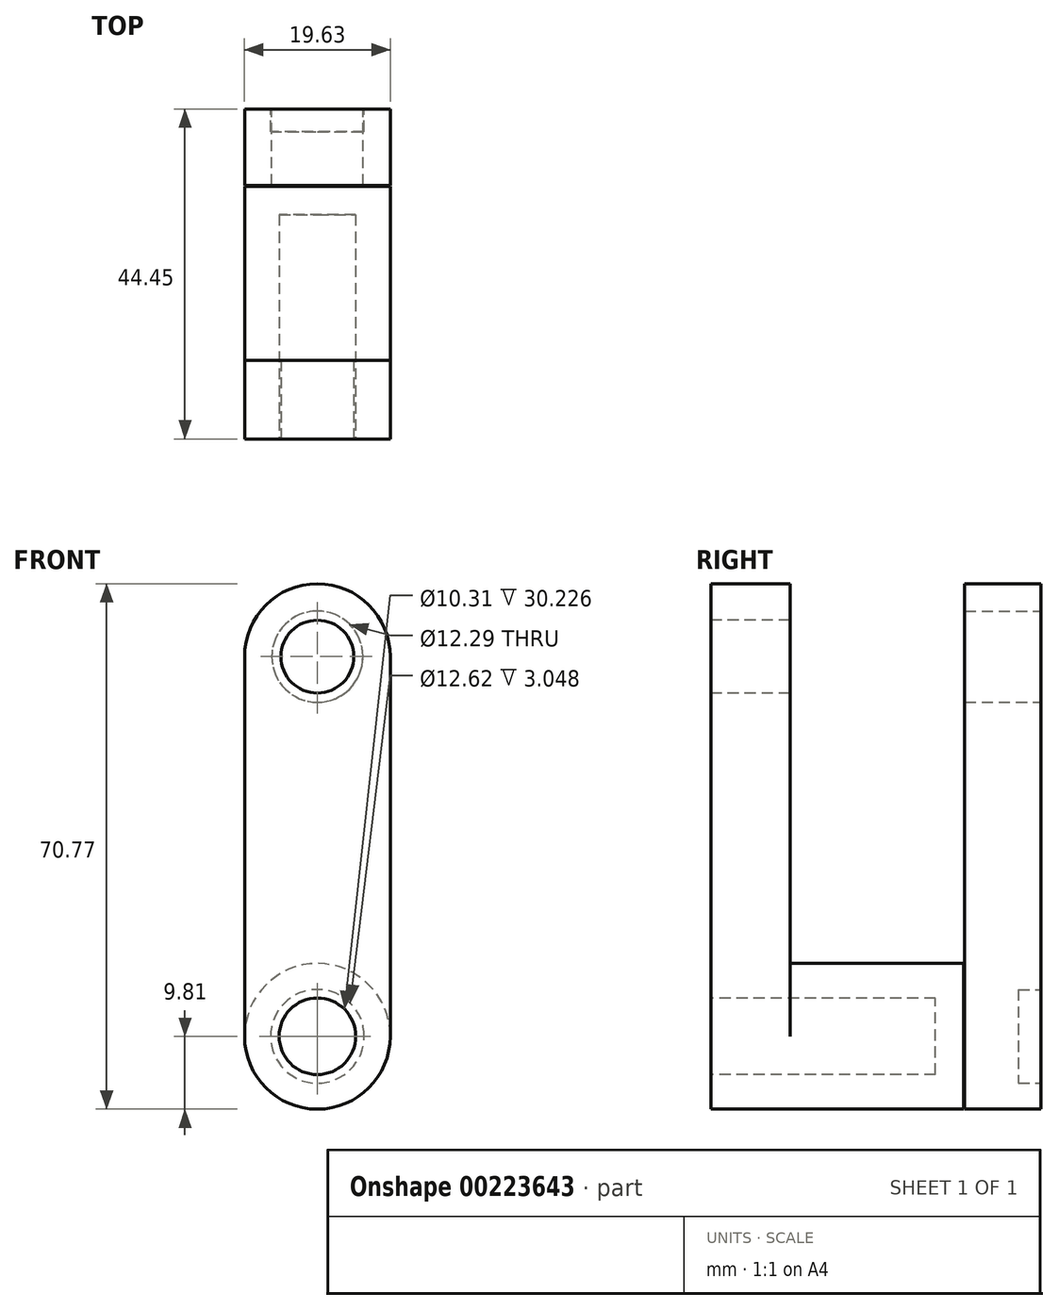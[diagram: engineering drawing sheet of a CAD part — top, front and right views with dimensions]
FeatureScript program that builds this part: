
annotation { "Feature Type Name" : "Feature", "Feature Type Description" : "" }
export const myFeature = defineFeature(function(context is Context, id is Id, definition is map)
    precondition{}
    {
        {
            var Q0;
            Q0=qCreatedBy(makeId("Front.planeOp"),FACE);
            var sketch = newSketch(context, id + "F0", { "sketchPlane" : qUnion([Q0])});
            skLineSegment(sketch, "E0", {"start": v(0, 0) * mm, "end": v(0, 51.15) * mm});
            skLineSegment(sketch, "E1", {"start": v(-19.63, 51.15) * mm, "end": v(-19.63, 0) * mm});
            skArc(sketch, "E2", {"start": v(-19.63, 51.15) * mm, "mid": v(-9.81, 60.96) * mm, "end": v(0, 51.15) * mm});
            skArc(sketch, "E3", {"start": v(-19.63, 0) * mm, "mid": v(-9.81, -9.81) * mm, "end": v(0, 0) * mm});
            skSolve(sketch);
        }
        {
            var Q0;
            Q0=makeQuery(id+"F0.imprint","IMPRINT",FACE,{"disambiguationData":[TD([[makeQuery(id+"F0.imprint","IMPRINT",EDGE,{"derivedFrom":sQuery(id+"F0.wireOp",EDGE,"E0")}),1.0]])]});
            extrude(context, id + "F1", {"entities" : qUnion([Q0]), "oppositeDirection" : true, "depth" : 44.45 * mm});
        }
        {
            var Q0;
            Q0=qCreatedBy(makeId("Right.planeOp"),FACE);
            var sketch = newSketch(context, id + "F2", { "sketchPlane" : qUnion([Q0])});
            skLineSegment(sketch, "E4.bottom", {"start": v(10.62, 64.08) * mm, "end": v(34.17, 64.08) * mm});
            skLineSegment(sketch, "E4.top", {"start": v(10.62, -13.05) * mm, "end": v(34.17, -13.05) * mm});
            skLineSegment(sketch, "E4.left", {"start": v(10.62, 64.08) * mm, "end": v(10.62, -13.05) * mm});
            skLineSegment(sketch, "E4.right", {"start": v(34.17, 64.08) * mm, "end": v(34.17, -13.05) * mm});
            skSolve(sketch);
        }
        {
            var Q0;
            Q0 = qSketchRegion(id + "F2", true);
            extrude(context, id + "F3", {"entities" : qUnion([Q0]), "operationType" : NewBodyOperationType.REMOVE, "oppositeDirection" : true, "depth" : 101.6 * mm});
        }
        {
            var Q0;
            Q0=makeQuery(id+"F1.opExtrude","CAP_FACE",FACE,{"disambiguationData":[OSD([sQuery(id+"F0.wireOp",EDGE,"E0"),sQuery(id+"F0.wireOp",EDGE,"E1"),sQuery(id+"F0.wireOp",EDGE,"E2"),sQuery(id+"F0.wireOp",EDGE,"E3")])],"isStart":true});
            var sketch = newSketch(context, id + "F4", { "sketchPlane" : qUnion([Q0])});
            skCircle(sketch, "E5", {"center": v(-9.81, 0) * mm, "radius": 4.02 * mm});
            skCircle(sketch, "E6", {"center": v(-9.81, 51.15) * mm, "radius": 4.9 * mm});
            skSolve(sketch);
        }
        {
            var Q0;
            Q0=makeQuery(id+"F4.imprint","IMPRINT",FACE,{"disambiguationData":[TD([[makeQuery(id+"F4.imprint","IMPRINT",EDGE,{"derivedFrom":sQuery(id+"F4.wireOp",EDGE,"E6")}),1.0]])]});
            extrude(context, id + "F5", {"entities" : qUnion([Q0]), "operationType" : NewBodyOperationType.REMOVE, "oppositeDirection" : true, "depth" : 74.93 * mm});
        }
        {
            var Q0;
            Q0=makeQuery(id+"F1.opExtrude","CAP_FACE",FACE,{"disambiguationData":[OSD([sQuery(id+"F0.wireOp",EDGE,"E0"),sQuery(id+"F0.wireOp",EDGE,"E1"),sQuery(id+"F0.wireOp",EDGE,"E2"),sQuery(id+"F0.wireOp",EDGE,"E3")])],"isStart":true});
            var sketch = newSketch(context, id + "F6", { "sketchPlane" : qUnion([Q0])});
            skArc(sketch, "E7", {"start": v(0, 0) * mm, "mid": v(-9.81, 9.81) * mm, "end": v(-19.63, 0) * mm});
            skSolve(sketch);
        }
        {
            var Q0;
            Q0=makeQuery(id+"F6.imprint","IMPRINT",FACE,{"disambiguationData":[TD([[makeQuery(id+"F6.imprint","IMPRINT",EDGE,{"derivedFrom":sQuery(id+"F6.wireOp",EDGE,"E7")}),1.0]])]});
            extrude(context, id + "F7", {"entities" : qUnion([Q0]), "operationType" : NewBodyOperationType.ADD, "oppositeDirection" : true, "depth" : 34.04 * mm});
        }
        {
            var Q0;
            Q0=makeQuery(id+"F1.opExtrude","CAP_FACE",FACE,{"disambiguationData":[OSD([sQuery(id+"F0.wireOp",EDGE,"E0"),sQuery(id+"F0.wireOp",EDGE,"E1"),sQuery(id+"F0.wireOp",EDGE,"E2"),sQuery(id+"F0.wireOp",EDGE,"E3")])],"isStart":true});
            var sketch = newSketch(context, id + "F8", { "sketchPlane" : qUnion([Q0])});
            skCircle(sketch, "E8", {"center": v(-9.81, 0) * mm, "radius": 5.16 * mm});
            skSolve(sketch);
        }
        {
            var Q0;
            Q0=makeQuery(id+"F8.imprint","IMPRINT",FACE,{"disambiguationData":[TD([[makeQuery(id+"F8.imprint","IMPRINT",EDGE,{"derivedFrom":sQuery(id+"F8.wireOp",EDGE,"E8")}),1.0]])]});
            extrude(context, id + "F9", {"entities" : qUnion([Q0]), "operationType" : NewBodyOperationType.REMOVE, "oppositeDirection" : true, "depth" : 30.23 * mm});
        }
        {
            var Q0;
            Q0=makeQuery(id+"F1.opExtrude","CAP_FACE",FACE,{"disambiguationData":[OSD([sQuery(id+"F0.wireOp",EDGE,"E0"),sQuery(id+"F0.wireOp",EDGE,"E1"),sQuery(id+"F0.wireOp",EDGE,"E2"),sQuery(id+"F0.wireOp",EDGE,"E3")])],"isStart":false});
            var sketch = newSketch(context, id + "F10", { "sketchPlane" : qUnion([Q0])});
            skCircle(sketch, "E9", {"center": v(9.81, 51.15) * mm, "radius": 6.15 * mm});
            skCircle(sketch, "E10", {"center": v(9.81, 0) * mm, "radius": 6.14 * mm});
            skSolve(sketch);
        }
        {
            var Q0;
            Q0=makeQuery(id+"F10.imprint","IMPRINT",FACE,{"disambiguationData":[TD([[makeQuery(id+"F10.imprint","IMPRINT",EDGE,{"derivedFrom":sQuery(id+"F10.wireOp",EDGE,"E9")}),1.0]])]});
            extrude(context, id + "F11", {"entities" : qUnion([Q0]), "operationType" : NewBodyOperationType.REMOVE, "oppositeDirection" : true, "depth" : 23.62 * mm});
        }
        {
            var Q0;
            Q0=makeQuery(id+"F1.opExtrude","CAP_FACE",FACE,{"disambiguationData":[OSD([sQuery(id+"F0.wireOp",EDGE,"E0"),sQuery(id+"F0.wireOp",EDGE,"E1"),sQuery(id+"F0.wireOp",EDGE,"E2"),sQuery(id+"F0.wireOp",EDGE,"E3")])],"isStart":false});
            var sketch = newSketch(context, id + "F12", { "sketchPlane" : qUnion([Q0])});
            skCircle(sketch, "E11", {"center": v(9.81, 0) * mm, "radius": 6.3 * mm});
            skSolve(sketch);
        }
        {
            var Q0;
            Q0=makeQuery(id+"F12.imprint","IMPRINT",FACE,{"disambiguationData":[TD([[makeQuery(id+"F12.imprint","IMPRINT",EDGE,{"derivedFrom":sQuery(id+"F12.wireOp",EDGE,"E11")}),1.0]])]});
            extrude(context, id + "F13", {"entities" : qUnion([Q0]), "operationType" : NewBodyOperationType.REMOVE, "oppositeDirection" : true, "depth" : 3.05 * mm});
        }
    });
